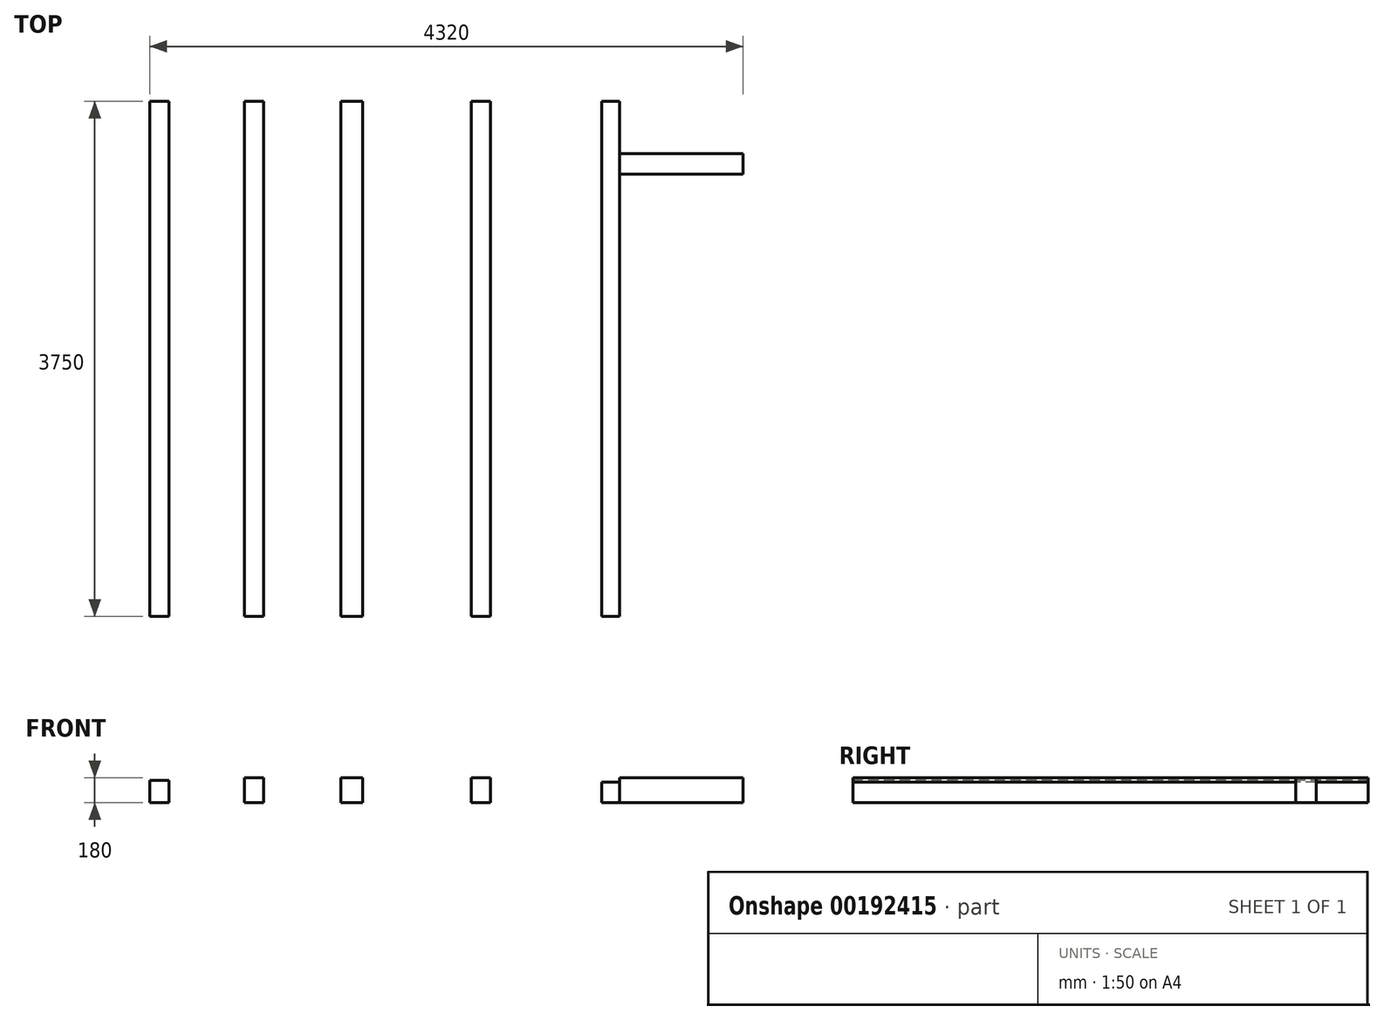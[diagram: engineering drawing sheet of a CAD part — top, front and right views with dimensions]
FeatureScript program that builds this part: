
annotation { "Feature Type Name" : "Feature", "Feature Type Description" : "" }
export const myFeature = defineFeature(function(context is Context, id is Id, definition is map)
    precondition{}
    {
        {
            var Q0;
            Q0=qCreatedBy(makeId("Top.planeOp"),FACE);
            var sketch = newSketch(context, id + "F0", { "sketchPlane" : qUnion([Q0])});
            skLineSegment(sketch, "E0.bottom", {"start": v(-70, 1875) * mm, "end": v(70, 1875) * mm});
            skLineSegment(sketch, "E0.top", {"start": v(-70, -1875) * mm, "end": v(70, -1875) * mm});
            skLineSegment(sketch, "E0.left", {"start": v(-70, 1875) * mm, "end": v(-70, -1875) * mm});
            skLineSegment(sketch, "E0.right", {"start": v(70, 1875) * mm, "end": v(70, -1875) * mm});
            skPoint(sketch, "E0.middle", {"position": v(0, 0) * mm});
            skLineSegment(sketch, "E1.bottom", {"start": v(880, 1875) * mm, "end": v(1010, 1875) * mm});
            skLineSegment(sketch, "E1.top", {"start": v(880, -1875) * mm, "end": v(1010, -1875) * mm});
            skLineSegment(sketch, "E1.left", {"start": v(880, 1875) * mm, "end": v(880, -1875) * mm});
            skLineSegment(sketch, "E1.right", {"start": v(1010, 1875) * mm, "end": v(1010, -1875) * mm});
            skLineSegment(sketch, "E2.bottom", {"start": v(-860, 1875) * mm, "end": v(-1020, 1875) * mm});
            skLineSegment(sketch, "E2.top", {"start": v(-860, -1875) * mm, "end": v(-1020, -1875) * mm});
            skLineSegment(sketch, "E2.left", {"start": v(-860, 1875) * mm, "end": v(-860, -1875) * mm});
            skLineSegment(sketch, "E2.right", {"start": v(-1020, 1875) * mm, "end": v(-1020, -1875) * mm});
            skLineSegment(sketch, "E3.bottom", {"start": v(-1580, 1875) * mm, "end": v(-1720, 1875) * mm});
            skLineSegment(sketch, "E3.top", {"start": v(-1580, -1875) * mm, "end": v(-1720, -1875) * mm});
            skLineSegment(sketch, "E3.left", {"start": v(-1580, 1875) * mm, "end": v(-1580, -1875) * mm});
            skLineSegment(sketch, "E3.right", {"start": v(-1720, 1875) * mm, "end": v(-1720, -1875) * mm});
            skLineSegment(sketch, "E4.bottom", {"start": v(-2270, 1875) * mm, "end": v(-2410, 1875) * mm});
            skLineSegment(sketch, "E4.top", {"start": v(-2270, -1875) * mm, "end": v(-2410, -1875) * mm});
            skLineSegment(sketch, "E4.left", {"start": v(-2270, 1875) * mm, "end": v(-2270, -1875) * mm});
            skLineSegment(sketch, "E4.right", {"start": v(-2410, 1875) * mm, "end": v(-2410, -1875) * mm});
            skLineSegment(sketch, "E5", {"start": v(1010, 1495) * mm, "end": v(1910, 1495) * mm});
            skLineSegment(sketch, "E6", {"start": v(1910, 1495) * mm, "end": v(1910, 1345) * mm});
            skLineSegment(sketch, "E7", {"start": v(1910, 1345) * mm, "end": v(1010, 1345) * mm});
            skLineSegment(sketch, "E8.bottom", {"start": v(1750, 1345) * mm, "end": v(1570, 1345) * mm});
            skLineSegment(sketch, "E8.top", {"start": v(1750, -1875) * mm, "end": v(1570, -1875) * mm});
            skLineSegment(sketch, "E8.left", {"start": v(1750, 1345) * mm, "end": v(1750, -1875) * mm});
            skLineSegment(sketch, "E8.right", {"start": v(1570, 1345) * mm, "end": v(1570, -1875) * mm});
            skSolve(sketch);
        }
        {
            var Q0;
            {var subQ1=sQuery(id+"F0.wireOp",EDGE,"E5");Q0=makeQuery(id+"F0.imprint","IMPRINT",FACE,{"disambiguationData":[TD([[makeQuery(id+"F0.imprint","IMPRINT",EDGE,{"derivedFrom":subQ1}),-1.0]])]});}
            var Q1;
            Q1=makeQuery(id+"F0.imprint","IMPRINT",FACE,{"disambiguationData":[TD([[makeQuery(id+"F0.imprint","IMPRINT",EDGE,{"derivedFrom":sQuery(id+"F0.wireOp",EDGE,"E8.bottom")}),1.0]])]});
            var Q2;
            Q2=makeQuery(id+"F0.imprint","IMPRINT",FACE,{"disambiguationData":[TD([[makeQuery(id+"F0.imprint","IMPRINT",EDGE,{"derivedFrom":sQuery(id+"F0.wireOp",EDGE,"E0.bottom")}),-1.0]])]});
            var Q3;
            Q3=makeQuery(id+"F0.imprint","IMPRINT",FACE,{"disambiguationData":[TD([[makeQuery(id+"F0.imprint","IMPRINT",EDGE,{"derivedFrom":sQuery(id+"F0.wireOp",EDGE,"E2.bottom")}),1.0]])]});
            var Q4;
            Q4=makeQuery(id+"F0.imprint","IMPRINT",FACE,{"disambiguationData":[TD([[makeQuery(id+"F0.imprint","IMPRINT",EDGE,{"derivedFrom":sQuery(id+"F0.wireOp",EDGE,"E3.bottom")}),1.0]])]});
            extrude(context, id + "F1", {"entities" : qUnion([Q0, Q1, Q2, Q3, Q4]), "depth" : 180 * mm});
        }
        {
            var Q0;
            {var subQ1=sQuery(id+"F0.wireOp",EDGE,"E1.bottom");Q0=makeQuery(id+"F0.imprint","IMPRINT",FACE,{"disambiguationData":[TD([[makeQuery(id+"F0.imprint","IMPRINT",EDGE,{"derivedFrom":subQ1}),-1.0]])]});}
            extrude(context, id + "F2", {"entities" : qUnion([Q0]), "operationType" : NewBodyOperationType.ADD, "depth" : 150 * mm});
        }
        {
            var Q0;
            Q0=makeQuery(id+"F0.imprint","IMPRINT",FACE,{"disambiguationData":[TD([[makeQuery(id+"F0.imprint","IMPRINT",EDGE,{"derivedFrom":sQuery(id+"F0.wireOp",EDGE,"E4.bottom")}),1.0]])]});
            extrude(context, id + "F3", {"entities" : qUnion([Q0]), "depth" : 160 * mm});
        }
    });
